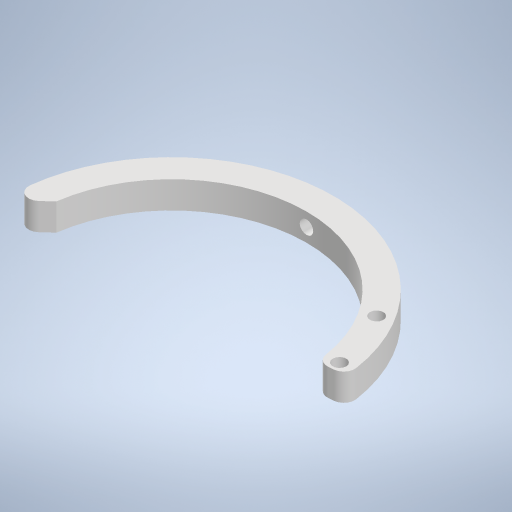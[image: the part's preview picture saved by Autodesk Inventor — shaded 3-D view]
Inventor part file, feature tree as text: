
AUTODESK INVENTOR PART (.ipt)
format: ipt  version: 2023 (Build 270158000, 158)  size: 282,112 bytes
history: native  units: mm
features: extrude x4, sketch x3, fillet x3, chamfer x1
ambient origin geometry x8: Origin, YZ Plane, XZ Plane, XY Plane, X Axis, Y Axis, Z Axis, Center Point
bodies: Solido1 (feature_tree)
feature tree (11):
  sketch  "Schizzo1"
  extrude  "Estrusione1"  Depth=100.0mm
  extrude  "Estrusione2"  Depth=10.0mm TaperAngle=0.0deg
  fillet  "Raccordo3"  Radius=5.0mm
  fillet  "Raccordo4"  Radius=2.5mm
  chamfer  "Smusso1"  Distance=2.5mm
  fillet  "Raccordo5"  [1 undecoded]
  extrude  "Estrusione3"  Depth=4.0mm
  extrude  "Estrusione5"  Depth=4.0mm
  sketch  "Schizzo2"
  sketch  "Schizzo4"
note: 1 required parameter value undecoded (feature->parameter linkage not recoverable at this tier; creation-order binding heuristic only, values carry confidence <= 0.55)
